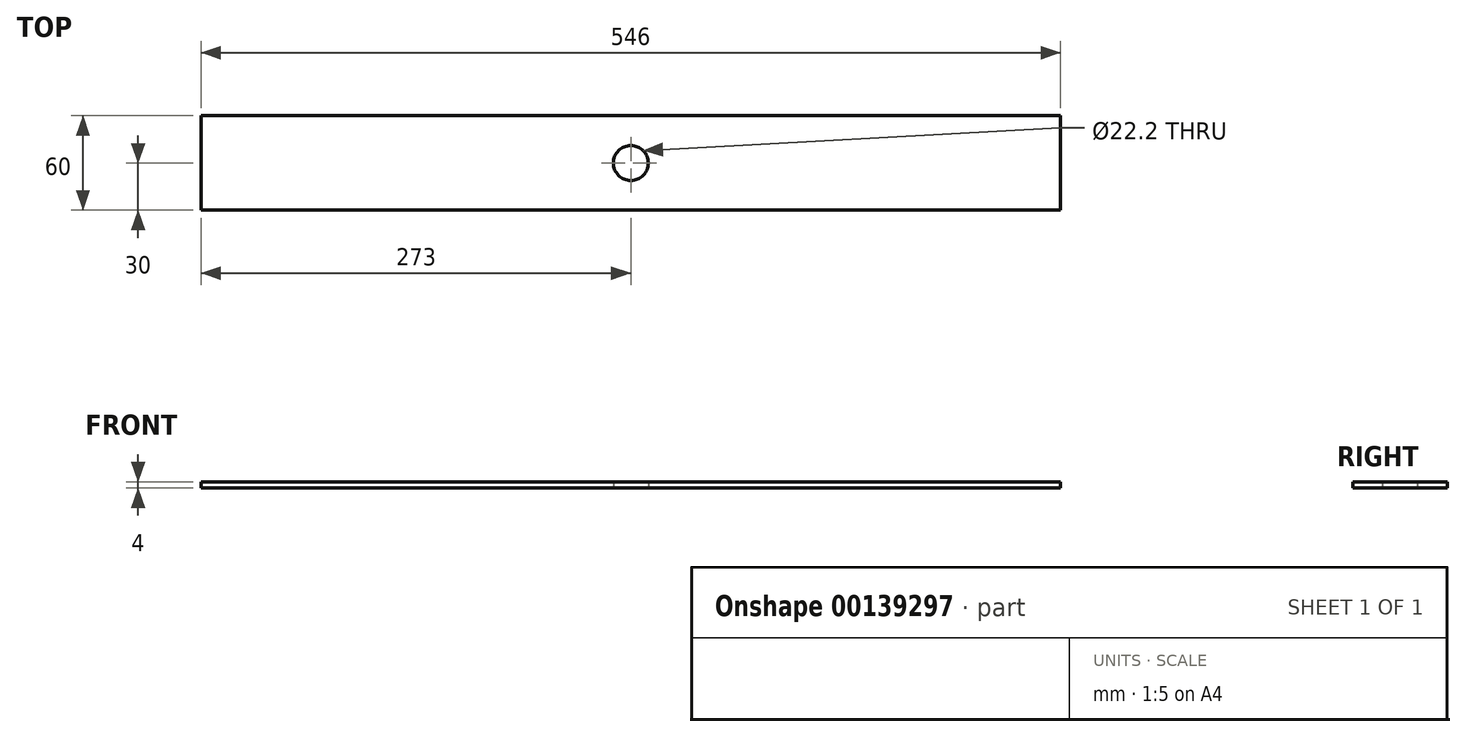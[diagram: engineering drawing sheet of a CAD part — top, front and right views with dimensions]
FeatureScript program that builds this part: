
annotation { "Feature Type Name" : "Feature", "Feature Type Description" : "" }
export const myFeature = defineFeature(function(context is Context, id is Id, definition is map)
    precondition{}
    {
        {
            var Q0;
            Q0=qCreatedBy(makeId("Top.planeOp"),FACE);
            var sketch = newSketch(context, id + "F0", { "sketchPlane" : qUnion([Q0])});
            skCircle(sketch, "E0", {"center": v(0, 0) * mm, "radius": 11.1 * mm});
            skLineSegment(sketch, "E1", {"start": v(0, 0) * mm, "end": v(11.1, 0) * mm});
            skLineSegment(sketch, "E2", {"start": v(0, 0) * mm, "end": v(-11.1, 0) * mm});
            skLineSegment(sketch, "E3", {"start": v(-273, 0) * mm, "end": v(-273, 30) * mm});
            skLineSegment(sketch, "E4", {"start": v(-273, 30) * mm, "end": v(273, 30) * mm});
            skLineSegment(sketch, "E5", {"start": v(273, 30) * mm, "end": v(273, -30) * mm});
            skLineSegment(sketch, "E6", {"start": v(273, -30) * mm, "end": v(-273, -30) * mm});
            skLineSegment(sketch, "E7", {"start": v(-273, -30) * mm, "end": v(-273, 0) * mm});
            skPoint(sketch, "E8.orphan", {"position": v(273, 0) * mm});
            skSolve(sketch);
        }
        {
            var Q0;
            Q0=makeQuery(id+"F0.imprint","IMPRINT",FACE,{"disambiguationData":[TD([[makeQuery(id+"F0.imprint","IMPRINT",EDGE,{"derivedFrom":sQuery(id+"F0.wireOp",EDGE,"E3")}),-1.0]])]});
            extrude(context, id + "F1", {"entities" : qUnion([Q0]), "depth" : 4 * mm});
        }
    });
